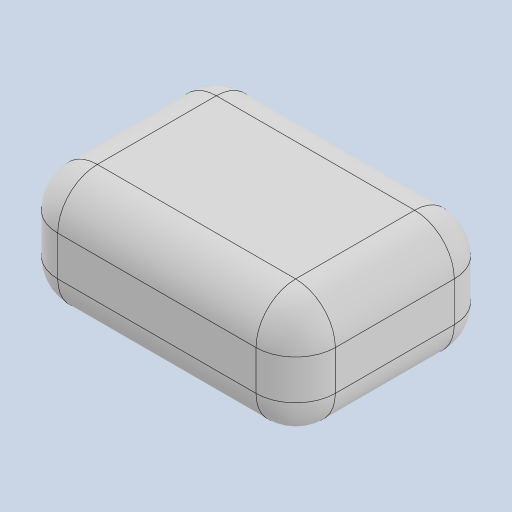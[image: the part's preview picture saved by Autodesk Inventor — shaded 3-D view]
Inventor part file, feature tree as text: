
AUTODESK INVENTOR PART (.ipt)
format: ipt  version: 2023 (Build 270158000, 158)  size: 141,312 bytes
history: native  units: mm
features: other x1, extrude x1, fillet x1, sketch x1
ambient origin geometry x8: Origin, YZ Plane, XZ Plane, XY Plane, X Axis, Y Axis, Z Axis, Center Point
bodies: Body1 (feature_tree)
feature tree (4):
  other  "ソリッド1"
  extrude  "押し出し1"  Depth=70.0mm
  fillet  "フィレット1"  Radius=50.0mm
  sketch  "スケッチ1"
